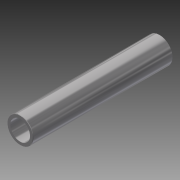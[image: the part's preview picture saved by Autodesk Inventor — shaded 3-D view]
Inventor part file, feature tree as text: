
AUTODESK INVENTOR PART (.ipt)
format: ipt  version: 2016 SP1 (Build 200210100, 210)  size: 109,568 bytes
history: native  units: in
note: dims shown in document units (in); Inventor stores cm internally (conversion verified against a paired STEP export)
features: other x21, revolve x1, sketch x1
ambient origin geometry x8: Origin, YZ Plane, XZ Plane, XY Plane, X Axis, Y Axis, Z Axis, Center Point
bodies: Solid1 (feature_tree)
feature tree (23):
  revolve  "Revolution1"  [1 undecoded]
  other  "cap_XY"
  other  "cap_YZ"
  other  "cap_ZX"
  other  "cap_X"
  other  "cap_Y"
  other  "cap_Z"
  other  "cap_Center"
  other  "ctr_XY"
  other  "ctr_YZ"
  other  "ctr_ZX"
  other  "ctr_X"
  other  "ctr_Y"
  other  "ctr_Z"
  other  "ctr_Center"
  other  "hd_XY"
  other  "hd_YZ"
  other  "hd_ZX"
  other  "hd_X"
  other  "hd_Y"
  other  "hd_Z"
  other  "hd_Center"
  sketch  "Sketch_2"  dims[d0=360.0deg d1=0.0in d2=0.0in]
note: 1 required parameter value undecoded (feature->parameter linkage not recoverable at this tier; creation-order binding heuristic only, values carry confidence <= 0.55)
